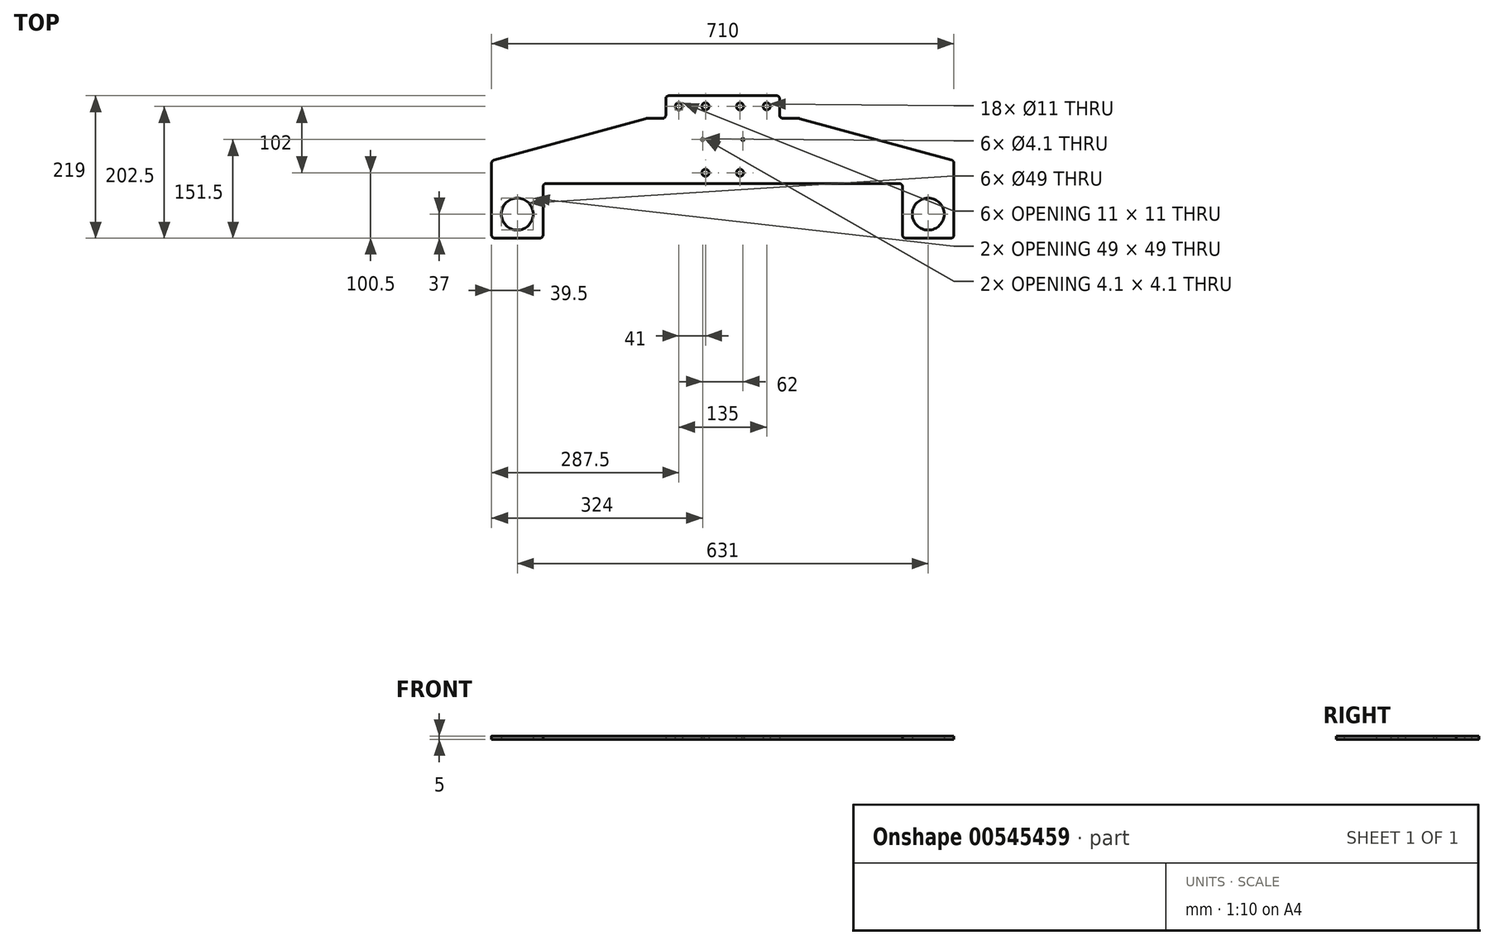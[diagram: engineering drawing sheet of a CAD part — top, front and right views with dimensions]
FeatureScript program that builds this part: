
annotation { "Feature Type Name" : "Feature", "Feature Type Description" : "" }
export const myFeature = defineFeature(function(context is Context, id is Id, definition is map)
    precondition{}
    {
        {
            var Q0;
            Q0=qCreatedBy(makeId("Top.planeOp"),FACE);
            var sketch = newSketch(context, id + "F0", { "sketchPlane" : qUnion([Q0])});
            skLineSegment(sketch, "E0", {"start": v(-117.5, 50) * mm, "end": v(117.5, 50) * mm});
            skLineSegment(sketch, "E1", {"start": v(-355, -50) * mm, "end": v(355, -50) * mm});
            skLineSegment(sketch, "E2", {"start": v(-355, -50) * mm, "end": v(-355, -134) * mm});
            skLineSegment(sketch, "E3", {"start": v(355, -50) * mm, "end": v(355, -134) * mm});
            skLineSegment(sketch, "E4", {"start": v(355, -134) * mm, "end": v(276, -134) * mm});
            skLineSegment(sketch, "E5", {"start": v(276, -134) * mm, "end": v(276, -50) * mm});
            skLineSegment(sketch, "E6", {"start": v(-355, -134) * mm, "end": v(-276, -134) * mm});
            skLineSegment(sketch, "E7", {"start": v(-276, -134) * mm, "end": v(-276, -50) * mm});
            skLineSegment(sketch, "E8", {"start": v(-355, -50) * mm, "end": v(-355, -15) * mm});
            skLineSegment(sketch, "E9", {"start": v(-355, -15) * mm, "end": v(-117.5, 50) * mm});
            skLineSegment(sketch, "E10", {"start": v(355, -50) * mm, "end": v(355, -15) * mm});
            skLineSegment(sketch, "E11", {"start": v(117.5, 50) * mm, "end": v(355, -15) * mm});
            skLineSegment(sketch, "E12", {"start": v(87.5, 50) * mm, "end": v(87.5, 85) * mm});
            skLineSegment(sketch, "E13", {"start": v(87.5, 85) * mm, "end": v(-87.5, 85) * mm});
            skLineSegment(sketch, "E14", {"start": v(-87.5, 85) * mm, "end": v(-87.5, 50) * mm});
            skSolve(sketch);
        }
        {
            var Q0;
            Q0=makeQuery(id+"F0.imprint","IMPRINT",FACE,{"disambiguationData":[TD([[makeQuery(id+"F0.imprint","IMPRINT",EDGE,{"derivedFrom":sQuery(id+"F0.wireOp",EDGE,"E0")}),-1.0]])]});
            var Q1;
            {var subQ0=sQuery(id+"F0.wireOp",EDGE,"E2");Q1=makeQuery(id+"F0.imprint","IMPRINT",FACE,{"disambiguationData":[TD([[makeQuery(id+"F0.imprint","IMPRINT",EDGE,{"derivedFrom":subQ0}),1.0]])]});}
            var Q2;
            {var subQ0=sQuery(id+"F0.wireOp",EDGE,"E3");Q2=makeQuery(id+"F0.imprint","IMPRINT",FACE,{"disambiguationData":[TD([[makeQuery(id+"F0.imprint","IMPRINT",EDGE,{"derivedFrom":subQ0}),-1.0]])]});}
            var Q3;
            {var subQ0=sQuery(id+"F0.wireOp",EDGE,"E12");Q3=makeQuery(id+"F0.imprint","IMPRINT",FACE,{"disambiguationData":[TD([[makeQuery(id+"F0.imprint","IMPRINT",EDGE,{"derivedFrom":subQ0}),1.0]])]});}
            extrude(context, id + "F1", {"entities" : qUnion([Q0, Q1, Q2, Q3]), "depth" : 5 * mm});
        }
        {
            var Q0;
            Q0=makeQuery(id+"F1.opExtrude","SWEPT_EDGE",EDGE,{"disambiguationData":[OSD([sQuery(id+"F0.wireOp",EDGE,"E2"),sQuery(id+"F0.wireOp",EDGE,"E6")])]});
            var Q1;
            Q1=makeQuery(id+"F1.opExtrude","SWEPT_EDGE",EDGE,{"disambiguationData":[OSD([sQuery(id+"F0.wireOp",EDGE,"E6"),sQuery(id+"F0.wireOp",EDGE,"E7")])]});
            var Q2;
            Q2=makeQuery(id+"F1.opExtrude","SWEPT_EDGE",EDGE,{"disambiguationData":[OSD([sQuery(id+"F0.wireOp",EDGE,"E4"),sQuery(id+"F0.wireOp",EDGE,"E5")])]});
            var Q3;
            Q3=makeQuery(id+"F1.opExtrude","SWEPT_EDGE",EDGE,{"disambiguationData":[OSD([sQuery(id+"F0.wireOp",EDGE,"E3"),sQuery(id+"F0.wireOp",EDGE,"E4")])]});
            var Q4;
            Q4=makeQuery(id+"F1.opExtrude","SWEPT_EDGE",EDGE,{"disambiguationData":[OSD([sQuery(id+"F0.wireOp",EDGE,"E10"),sQuery(id+"F0.wireOp",EDGE,"E11")])]});
            var Q5;
            Q5=makeQuery(id+"F1.opExtrude","SWEPT_EDGE",EDGE,{"disambiguationData":[OSD([sQuery(id+"F0.wireOp",EDGE,"E8"),sQuery(id+"F0.wireOp",EDGE,"E9")])]});
            var Q6;
            Q6=makeQuery(id+"F1.opExtrude","SWEPT_EDGE",EDGE,{"disambiguationData":[OSD([sQuery(id+"F0.wireOp",EDGE,"E1"),sQuery(id+"F0.wireOp",EDGE,"E7")])]});
            var Q7;
            Q7=makeQuery(id+"F1.opExtrude","SWEPT_EDGE",EDGE,{"disambiguationData":[OSD([sQuery(id+"F0.wireOp",EDGE,"E1"),sQuery(id+"F0.wireOp",EDGE,"E5")])]});
            var Q8;
            Q8=makeQuery(id+"F1.opExtrude","SWEPT_EDGE",EDGE,{"disambiguationData":[OSD([sQuery(id+"F0.wireOp",EDGE,"E0"),sQuery(id+"F0.wireOp",EDGE,"E14")])]});
            var Q9;
            Q9=makeQuery(id+"F1.opExtrude","SWEPT_EDGE",EDGE,{"disambiguationData":[OSD([sQuery(id+"F0.wireOp",EDGE,"E13"),sQuery(id+"F0.wireOp",EDGE,"E14")])]});
            var Q10;
            Q10=makeQuery(id+"F1.opExtrude","SWEPT_EDGE",EDGE,{"disambiguationData":[OSD([sQuery(id+"F0.wireOp",EDGE,"E12"),sQuery(id+"F0.wireOp",EDGE,"E13")])]});
            var Q11;
            Q11=makeQuery(id+"F1.opExtrude","SWEPT_EDGE",EDGE,{"disambiguationData":[OSD([sQuery(id+"F0.wireOp",EDGE,"E0"),sQuery(id+"F0.wireOp",EDGE,"E12")])]});
            fillet(context, id + "F2", {"entities" : qUnion([Q0, Q1, Q2, Q3, Q4, Q5, Q6, Q7, Q8, Q9, Q10, Q11]), "radius" : 5 * mm, "tangentPropagation" : true, "allowEdgeOverflow" : false});
        }
        {
            var Q0;
            Q0=makeQuery(id+"F1.opExtrude","SWEPT_EDGE",EDGE,{"disambiguationData":[OSD([sQuery(id+"F0.wireOp",EDGE,"E0"),sQuery(id+"F0.wireOp",EDGE,"E11")])]});
            var Q1;
            Q1=makeQuery(id+"F1.opExtrude","SWEPT_EDGE",EDGE,{"disambiguationData":[OSD([sQuery(id+"F0.wireOp",EDGE,"E0"),sQuery(id+"F0.wireOp",EDGE,"E9")])]});
            fillet(context, id + "F3", {"entities" : qUnion([Q0, Q1]), "radius" : 5 * mm, "tangentPropagation" : true, "allowEdgeOverflow" : false});
        }
        {
            var Q0;
            Q0=qCreatedBy(makeId("Top.planeOp"),FACE);
            var sketch = newSketch(context, id + "F4", { "sketchPlane" : qUnion([Q0])});
            skCircle(sketch, "E15", {"center": v(-67.5, 68.5) * mm, "radius": 5.5 * mm});
            skCircle(sketch, "E16", {"center": v(67.5, 68.5) * mm, "radius": 5.5 * mm});
            skCircle(sketch, "E17", {"center": v(-26.5, 68.5) * mm, "radius": 4.94 * mm});
            skCircle(sketch, "E18", {"center": v(26.5, 68.5) * mm, "radius": 7.16 * mm});
            skCircle(sketch, "E19", {"center": v(26.5, -33.5) * mm, "radius": 4.26 * mm});
            skCircle(sketch, "E20", {"center": v(-26.5, -33.5) * mm, "radius": 5.26 * mm});
            skSolve(sketch);
        }
        {
            var Q0;
            Q0=qCreatedBy(makeId("Top.planeOp"),FACE);
            var sketch = newSketch(context, id + "F5", { "sketchPlane" : qUnion([Q0])});
            skCircle(sketch, "E21", {"center": v(-31, 17.5) * mm, "radius": 4.53 * mm});
            skCircle(sketch, "E22", {"center": v(31, 17.5) * mm, "radius": 4.22 * mm});
            skSolve(sketch);
        }
        {
            var Q0;
            Q0=sQuery(id+"F5.wireOp",VERTEX,"E21.center");
            var Q1;
            Q1=sQuery(id+"F5.wireOp",VERTEX,"E22.center");
            var Q2;
            Q2=makeQuery(id+"F1.opExtrude","SWEPT_BODY",BODY,{"disambiguationData":[OSD([sQuery(id+"F0.wireOp",EDGE,"E0"),sQuery(id+"F0.wireOp",EDGE,"E1"),sQuery(id+"F0.wireOp",EDGE,"E2"),sQuery(id+"F0.wireOp",EDGE,"E3"),sQuery(id+"F0.wireOp",EDGE,"E4"),sQuery(id+"F0.wireOp",EDGE,"E5"),sQuery(id+"F0.wireOp",EDGE,"E6"),sQuery(id+"F0.wireOp",EDGE,"E7"),sQuery(id+"F0.wireOp",EDGE,"E8"),sQuery(id+"F0.wireOp",EDGE,"E9"),sQuery(id+"F0.wireOp",EDGE,"E10"),sQuery(id+"F0.wireOp",EDGE,"E11")])]});
            hole(context, id + "F6", {"style" : HoleStyle.SIMPLE, "endStyle" : HoleEndStyle.THROUGH, "oppositeDirection" : true, "holeDiameter" : 4.1 * mm, "tappedDepth" : 12 * mm, "tapClearance" : 3, "locations" : qUnion([Q0, Q1]), "scope" : qUnion([Q2])});
        }
        {
            var Q0;
            Q0=qCreatedBy(makeId("Top.planeOp"),FACE);
            var sketch = newSketch(context, id + "F7", { "sketchPlane" : qUnion([Q0])});
            skCircle(sketch, "E23", {"center": v(-315.5, -97) * mm, "radius": 11.57 * mm});
            skCircle(sketch, "E24", {"center": v(315.5, -97) * mm, "radius": 8.32 * mm});
            skSolve(sketch);
        }
        {
            var Q0;
            Q0=sQuery(id+"F7.wireOp",VERTEX,"E23.center");
            var Q1;
            Q1=sQuery(id+"F7.wireOp",VERTEX,"E24.center");
            var Q2;
            Q2=makeQuery(id+"F1.opExtrude","SWEPT_BODY",BODY,{"disambiguationData":[OSD([sQuery(id+"F0.wireOp",EDGE,"E0"),sQuery(id+"F0.wireOp",EDGE,"E1"),sQuery(id+"F0.wireOp",EDGE,"E2"),sQuery(id+"F0.wireOp",EDGE,"E3"),sQuery(id+"F0.wireOp",EDGE,"E4"),sQuery(id+"F0.wireOp",EDGE,"E5"),sQuery(id+"F0.wireOp",EDGE,"E6"),sQuery(id+"F0.wireOp",EDGE,"E7"),sQuery(id+"F0.wireOp",EDGE,"E8"),sQuery(id+"F0.wireOp",EDGE,"E9"),sQuery(id+"F0.wireOp",EDGE,"E10"),sQuery(id+"F0.wireOp",EDGE,"E11")])]});
            hole(context, id + "F8", {"style" : HoleStyle.SIMPLE, "endStyle" : HoleEndStyle.THROUGH, "oppositeDirection" : true, "holeDiameter" : 49 * mm, "tappedDepth" : 12 * mm, "tapClearance" : 3, "locations" : qUnion([Q0, Q1]), "scope" : qUnion([Q2])});
        }
        {
            var Q0;
            Q0=sQuery(id+"F4.wireOp",VERTEX,"E15.center");
            var Q1;
            Q1=sQuery(id+"F4.wireOp",VERTEX,"E16.center");
            var Q2;
            Q2=sQuery(id+"F4.wireOp",VERTEX,"V0FrDJi0-5RUE-7QYn-pTRS-WBAOulQvoWCY.center");
            var Q3;
            Q3=sQuery(id+"F4.wireOp",VERTEX,"H4CvWDiY-vmEf-QlYQ-u3RQ-upoS9Z0ZfnDX.center");
            var Q4;
            Q4=sQuery(id+"F4.wireOp",VERTEX,"E17.center");
            var Q5;
            Q5=sQuery(id+"F4.wireOp",VERTEX,"E18.center");
            var Q6;
            Q6=sQuery(id+"F4.wireOp",VERTEX,"E20.center");
            var Q7;
            Q7=sQuery(id+"F4.wireOp",VERTEX,"E19.center");
            var Q8;
            Q8=makeQuery(id+"F1.opExtrude","SWEPT_BODY",BODY,{"disambiguationData":[OSD([sQuery(id+"F0.wireOp",EDGE,"E0"),sQuery(id+"F0.wireOp",EDGE,"E1"),sQuery(id+"F0.wireOp",EDGE,"E2"),sQuery(id+"F0.wireOp",EDGE,"E3"),sQuery(id+"F0.wireOp",EDGE,"E4"),sQuery(id+"F0.wireOp",EDGE,"E5"),sQuery(id+"F0.wireOp",EDGE,"E6"),sQuery(id+"F0.wireOp",EDGE,"E7"),sQuery(id+"F0.wireOp",EDGE,"E8"),sQuery(id+"F0.wireOp",EDGE,"E9"),sQuery(id+"F0.wireOp",EDGE,"E10"),sQuery(id+"F0.wireOp",EDGE,"E11"),sQuery(id+"F0.wireOp",EDGE,"E12"),sQuery(id+"F0.wireOp",EDGE,"E13"),sQuery(id+"F0.wireOp",EDGE,"E14")])]});
            hole(context, id + "F9", {"style" : HoleStyle.SIMPLE, "endStyle" : HoleEndStyle.THROUGH, "oppositeDirection" : true, "standardTappedOrClearance" : lookupTablePath({ "standard" : "ISO", "fit" : "Normal", "size" : "M10", "type" : "Clearance" }), "standardBlindInLast" : lookupTablePath({ "fit" : "Standard", "standard" : "ISO", "size" : "M10", "type" : "Clearance" }), "holeDiameter" : 11 * mm, "tappedDepth" : 12 * mm, "tapClearance" : 3, "locations" : qUnion([Q0, Q1, Q2, Q3, Q4, Q5, Q6, Q7]), "scope" : qUnion([Q8])});
        }
    });
